# Revit family: TYCO-FPP-Fireclass- FC32-1 panel
name_source: partatom
category: Electrical Fixtures
revit_build: Autodesk Revit 2014 (Build: 20130308_1515(x64)
units: mm (PartAtom-declared; Revit-internal decimal feet)

## types (1)
- TYCO-FPP-Fireclass- FC32-1 panel
    Auxiliary relay quantity = 1 Fire, 1 Fault
    BODY = RAL
    Charger Size = 2.5A
    Conventional Sounder circuits = 2 x 2Amp
    D = 156 mm
    DISPLAY = DIS
    Description = FireClass 32 One Loop Addressable Panel
    EMC/RFI = EN50130-4 & EN61000-6-3
    H = 370 mm
    Humidity = 90% relative Humidity
    IP rating = IP30
    Input Current = 0.9A
    Keynote = The FireClass 32 digital addressable panel has been designed to work with FireClass protocol devices.
    Manufacturer = Tyco
    Max Battery Size = 2 x 12V 12Ah
    Model = Fireclass - 557.200.701
    Operating Temp = -5ºC + 40ºC
    Output ports = RS232, RS485
    SWPAD = SWPAD
    Storage Temp = -20ºC + 70ºC
    Supply Voltage = 230VAC 50/60 Hz 24VDC
    Type Comments = Permanently displays system status
    URL = https://fireclass.co.uk
    W = 325 mm

## geometry (parser evidence)
native form markers: Sweep x1
no freeform markers — native parametric forms only
